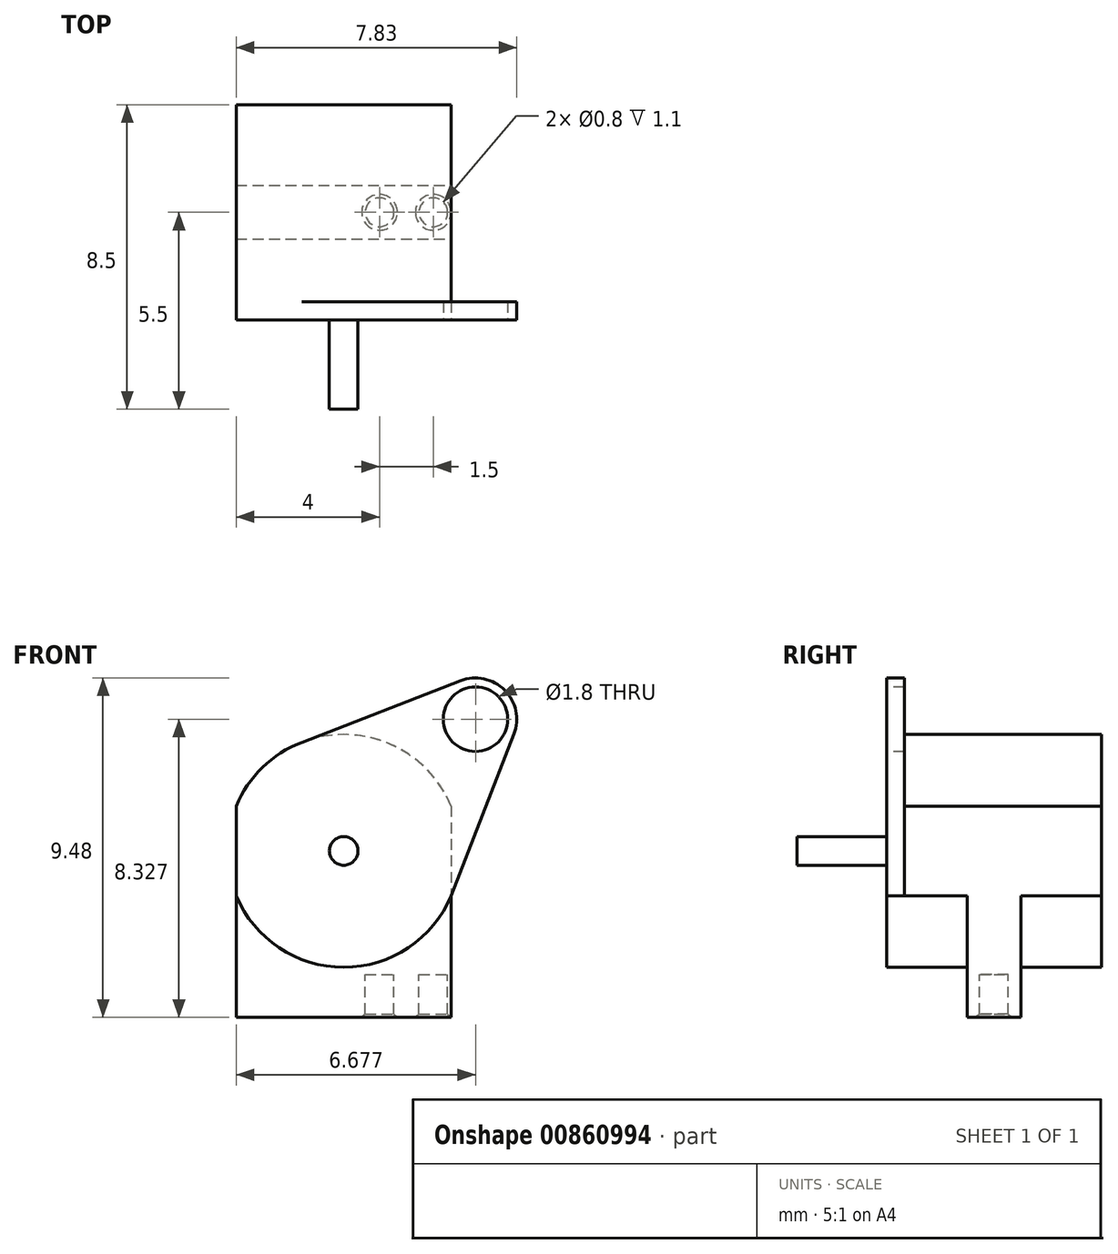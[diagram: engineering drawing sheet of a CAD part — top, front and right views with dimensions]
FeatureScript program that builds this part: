
annotation { "Feature Type Name" : "Feature", "Feature Type Description" : "" }
export const myFeature = defineFeature(function(context is Context, id is Id, definition is map)
    precondition{}
    {
        {
            var Q0;
            Q0=qCreatedBy(makeId("Front.planeOp"),FACE);
            var sketch = newSketch(context, id + "F0", { "sketchPlane" : qUnion([Q0])});
            skLineSegment(sketch, "E0.bottom", {"start": v(-3, 3.25) * mm, "end": v(3, 3.25) * mm});
            skLineSegment(sketch, "E0.top", {"start": v(-3, -3.25) * mm, "end": v(3, -3.25) * mm});
            skLineSegment(sketch, "E0.left", {"start": v(-3, 3.25) * mm, "end": v(-3, -3.25) * mm});
            skLineSegment(sketch, "E0.right", {"start": v(3, 3.25) * mm, "end": v(3, -3.25) * mm});
            skLineSegment(sketch, "E1", {"start": v(-3.3, 1.25) * mm, "end": v(3.34, 1.25) * mm, "construction": true});
            skPoint(sketch, "E2", {"position": v(0, 3.25) * mm});
            skPoint(sketch, "E3", {"position": v(-3, 1.25) * mm});
            skPoint(sketch, "E4", {"position": v(3, 1.25) * mm});
            skArc(sketch, "E5", {"start": v(3, 1.25) * mm, "mid": v(0, 3.25) * mm, "end": v(-3, 1.25) * mm});
            skArc(sketch, "E6.MirrorCS", {"start": v(3, -1.25) * mm, "mid": v(0, -3.25) * mm, "end": v(-3, -1.25) * mm});
            skSolve(sketch);
        }
        {
            var Q0;
            {var subQ0=sQuery(id+"F0.wireOp",EDGE,"E5");var subQ1=sQuery(id+"F0.wireOp",EDGE,"E0.left");var subQ2=makeQuery(id+"F0.imprint","INTERSECT",VERTEX,{"derivedFrom":[subQ1,subQ0]});Q0=makeQuery(id+"F0.imprint","IMPRINT",FACE,{"disambiguationData":[TD([[makeQuery(id+"F0.imprint","IMPRINT",EDGE,{"disambiguationData":[TD([[subQ2,-1.0]])],"derivedFrom":subQ1}),1.0]])]});}
            extrude(context, id + "F1", {"entities" : qUnion([Q0]), "oppositeDirection" : true, "depth" : 6 * mm, "offsetDistance" : 25 * mm});
        }
        {
            var Q0;
            Q0=makeQuery(id+"F1.opExtrude","CAP_FACE",FACE,{"disambiguationData":[OSD([sQuery(id+"F0.wireOp",EDGE,"E0.left"),sQuery(id+"F0.wireOp",EDGE,"E0.right"),sQuery(id+"F0.wireOp",EDGE,"E5"),sQuery(id+"F0.wireOp",EDGE,"E6.MirrorCS")])],"isStart":true});
            var sketch = newSketch(context, id + "F2", { "sketchPlane" : qUnion([Q0])});
            skCircle(sketch, "E7", {"center": v(3.64, 2.78) * mm, "radius": 0.9 * mm});
            skCircle(sketch, "E8", {"center": v(0, 0) * mm, "radius": 0.4 * mm});
            skSolve(sketch);
        }
        {
            var Q0;
            Q0=makeQuery(id+"F2.imprint","IMPRINT",FACE,{"disambiguationData":[TD([[makeQuery(id+"F2.imprint","IMPRINT",EDGE,{"derivedFrom":sQuery(id+"F2.wireOp",EDGE,"E8")}),1.0]])]});
            extrude(context, id + "F3", {"entities" : qUnion([Q0]), "operationType" : NewBodyOperationType.ADD, "depth" : 2.5 * mm, "offsetDistance" : 25 * mm});
        }
        {
            var Q0;
            Q0=makeQuery(id+"F1.opExtrude","CAP_FACE",FACE,{"disambiguationData":[OSD([sQuery(id+"F0.wireOp",EDGE,"E0.left"),sQuery(id+"F0.wireOp",EDGE,"E0.right"),sQuery(id+"F0.wireOp",EDGE,"E5"),sQuery(id+"F0.wireOp",EDGE,"E6.MirrorCS")])],"isStart":true});
            var sketch = newSketch(context, id + "F4", { "sketchPlane" : qUnion([Q0])});
            skCircle(sketch, "E9", {"center": v(3.68, 3.68) * mm, "radius": 0.9 * mm});
            skLineSegment(sketch, "E10", {"start": v(0, 0) * mm, "end": v(3.68, 3.68) * mm, "construction": true});
            skCircle(sketch, "E11", {"center": v(3.68, 3.68) * mm, "radius": 1.15 * mm});
            skLineSegment(sketch, "E12", {"start": v(-11.48, -0.96) * mm, "end": v(17.23, 10.16) * mm, "construction": true});
            skLineSegment(sketch, "E13", {"start": v(-1.08, -11.78) * mm, "end": v(6.47, 7.7) * mm, "construction": true});
            skPoint(sketch, "E14", {"position": v(-1.17, 3.03) * mm});
            skPoint(sketch, "E15", {"position": v(3, -1.25) * mm});
            skPoint(sketch, "E16", {"position": v(4.75, 3.26) * mm});
            skPoint(sketch, "E17", {"position": v(3.26, 4.75) * mm});
            skLineSegment(sketch, "E18", {"start": v(-1.17, 3.03) * mm, "end": v(3.26, 4.75) * mm});
            skLineSegment(sketch, "E19", {"start": v(3, -1.25) * mm, "end": v(4.75, 3.26) * mm});
            skSolve(sketch);
        }
        {
            var Q0;
            {var subQ1=sQuery(id+"F4.wireOp",EDGE,"E18");Q0=makeQuery(id+"F4.imprint","IMPRINT",FACE,{"disambiguationData":[TD([[makeQuery(id+"F4.imprint","IMPRINT",EDGE,{"derivedFrom":subQ1}),-1.0]])]});}
            var Q1;
            Q1=makeQuery(id+"F4.imprint","IMPRINT",FACE,{"disambiguationData":[TD([[makeQuery(id+"F4.imprint","IMPRINT",EDGE,{"derivedFrom":sQuery(id+"F4.wireOp",EDGE,"E9")}),-1.0]])]});
            extrude(context, id + "F5", {"entities" : qUnion([Q0, Q1]), "operationType" : NewBodyOperationType.ADD, "oppositeDirection" : true, "depth" : 0.5 * mm, "offsetDistance" : 25 * mm});
        }
        {
            var Q0;
            Q0=makeQuery(id+"F1.opExtrude","SWEPT_BODY",BODY,{"disambiguationData":[OSD([sQuery(id+"F0.wireOp",EDGE,"E0.left"),sQuery(id+"F0.wireOp",EDGE,"E0.right"),sQuery(id+"F0.wireOp",EDGE,"E5"),sQuery(id+"F0.wireOp",EDGE,"E6.MirrorCS")])]});
            transform(context, id + "F6", {"entities" : qUnion([Q0]), "transformType" : TransformType.TRANSLATION_3D, "dx" : 0 * mm, "dy" : -3 * mm, "dz" : 0 * mm, "makeCopy" : false});
        }
        {
            var Q0;
            Q0=qCreatedBy(makeId("Front.planeOp"),FACE);
            var sketch = newSketch(context, id + "F7", { "sketchPlane" : qUnion([Q0])});
            skLineSegment(sketch, "E20.bottom", {"start": v(-3, -3.45) * mm, "end": v(3, -3.45) * mm});
            skLineSegment(sketch, "E20.top", {"start": v(-3, -1.25) * mm, "end": v(3, -1.25) * mm});
            skLineSegment(sketch, "E20.left", {"start": v(-3, -3.45) * mm, "end": v(-3, -1.25) * mm});
            skLineSegment(sketch, "E20.right", {"start": v(3, -3.45) * mm, "end": v(3, -1.25) * mm});
            skSolve(sketch);
        }
        {
            var Q0;
            Q0=makeQuery(id+"F7.imprint","IMPRINT",FACE,{"disambiguationData":[TD([[makeQuery(id+"F7.imprint","IMPRINT",EDGE,{"derivedFrom":sQuery(id+"F7.wireOp",EDGE,"E20.bottom")}),1.0]])]});
            extrude(context, id + "F8", {"entities" : qUnion([Q0]), "operationType" : NewBodyOperationType.ADD, "endBound" : BoundingType.SYMMETRIC, "depth" : 1.5 * mm, "offsetDistance" : 25 * mm});
        }
        {
            var Q0;
            Q0=makeQuery(id+"F8.opExtrude","SWEPT_FACE",FACE,{"disambiguationData":[OSD([sQuery(id+"F7.wireOp",EDGE,"E20.bottom")])]});
            var sketch = newSketch(context, id + "F9", { "sketchPlane" : qUnion([Q0])});
            skCircle(sketch, "E21", {"center": v(-1, 0) * mm, "radius": 0.4 * mm});
            skCircle(sketch, "E22", {"center": v(-2.5, 0) * mm, "radius": 0.4 * mm});
            skCircle(sketch, "E23.MirrorC", {"center": v(2.5, 0) * mm, "radius": 0.4 * mm});
            skCircle(sketch, "E24.MirrorC", {"center": v(1, 0) * mm, "radius": 0.4 * mm});
            skSolve(sketch);
        }
        {
            var Q0;
            Q0=makeQuery(id+"F9.imprint","IMPRINT",FACE,{"disambiguationData":[TD([[makeQuery(id+"F9.imprint","IMPRINT",EDGE,{"derivedFrom":sQuery(id+"F9.wireOp",EDGE,"E22")}),1.0]])]});
            var Q1;
            Q1=makeQuery(id+"F9.imprint","IMPRINT",FACE,{"disambiguationData":[TD([[makeQuery(id+"F9.imprint","IMPRINT",EDGE,{"derivedFrom":sQuery(id+"F9.wireOp",EDGE,"E21")}),1.0]])]});
            var Q2;
            Q2=makeQuery(id+"F9.imprint","IMPRINT",FACE,{"disambiguationData":[TD([[makeQuery(id+"F9.imprint","IMPRINT",EDGE,{"derivedFrom":sQuery(id+"F9.wireOp",EDGE,"E24.MirrorC")}),-1.0]])]});
            var Q3;
            Q3=makeQuery(id+"F9.imprint","IMPRINT",FACE,{"disambiguationData":[TD([[makeQuery(id+"F9.imprint","IMPRINT",EDGE,{"derivedFrom":sQuery(id+"F9.wireOp",EDGE,"E23.MirrorC")}),-1.0]])]});
            extrude(context, id + "F10", {"entities" : qUnion([Q0, Q1, Q2, Q3]), "operationType" : NewBodyOperationType.ADD, "depth" : 1.2 * mm, "offsetDistance" : 25 * mm});
        }
        {
            var Q0;
            Q0=makeQuery(id+"F10.opExtrude","CAP_EDGE",EDGE,{"disambiguationData":[OSD([sQuery(id+"F9.wireOp",EDGE,"E22")])],"isStart":false});
            var Q1;
            Q1=makeQuery(id+"F10.opExtrude","CAP_EDGE",EDGE,{"disambiguationData":[OSD([sQuery(id+"F9.wireOp",EDGE,"E21")])],"isStart":false});
            var Q2;
            Q2=makeQuery(id+"F10.opExtrude","CAP_EDGE",EDGE,{"disambiguationData":[OSD([sQuery(id+"F9.wireOp",EDGE,"E24.MirrorC")])],"isStart":false});
            var Q3;
            Q3=makeQuery(id+"F10.opExtrude","CAP_EDGE",EDGE,{"disambiguationData":[OSD([sQuery(id+"F9.wireOp",EDGE,"E23.MirrorC")])],"isStart":false});
            chamfer(context, id + "F11", {"entities" : qUnion([Q0, Q1, Q2, Q3]), "width" : 0.1 * mm, "tangentPropagation" : true});
        }
    });
